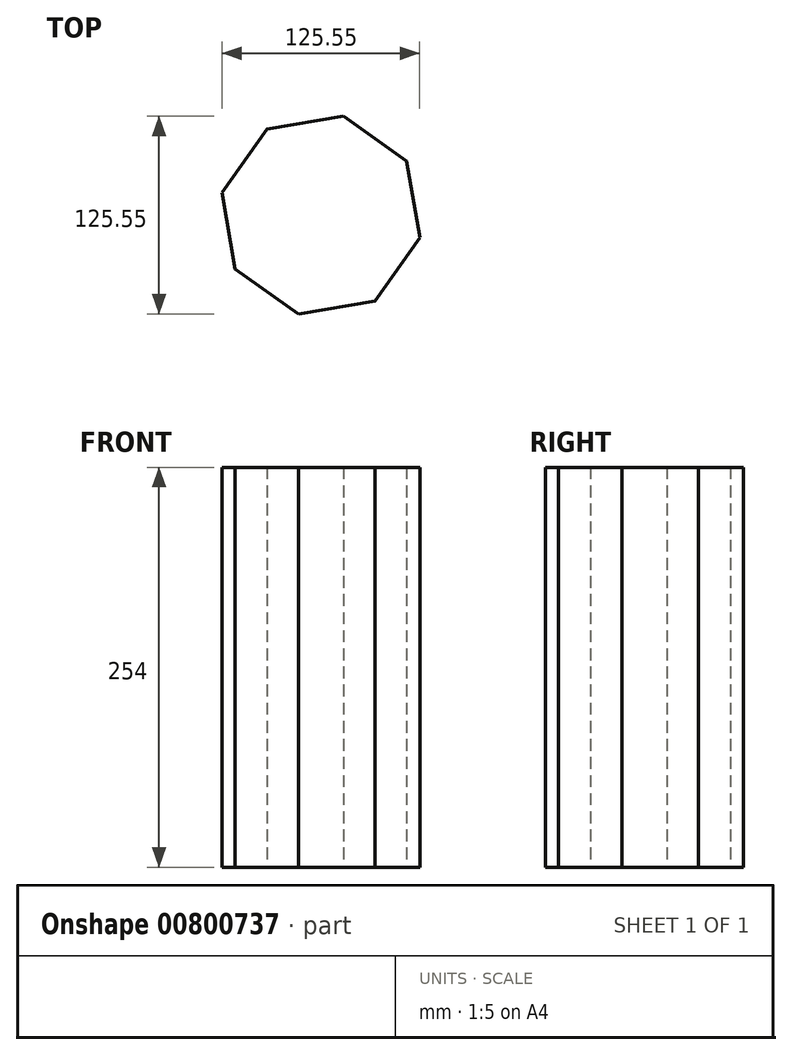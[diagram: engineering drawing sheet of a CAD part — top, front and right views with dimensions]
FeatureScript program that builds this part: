
annotation { "Feature Type Name" : "Feature", "Feature Type Description" : "" }
export const myFeature = defineFeature(function(context is Context, id is Id, definition is map)
    precondition{}
    {
        {
            var Q0;
            Q0=qCreatedBy(makeId("Top.planeOp"),FACE);
            var sketch = newSketch(context, id + "F0", { "sketchPlane" : qUnion([Q0])});
            skCircle(sketch, "E0.cCircle", {"center": v(-30.55, -6.8) * mm, "radius": 59.5 * mm, "construction": true});
            skLineSegment(sketch, "E0.0", {"start": v(-16.2, 55.98) * mm, "end": v(23.98, 27.44) * mm});
            skLineSegment(sketch, "E0.1", {"start": v(23.98, 27.44) * mm, "end": v(32.22, -21.15) * mm});
            skLineSegment(sketch, "E0.2", {"start": v(32.22, -21.15) * mm, "end": v(3.69, -61.33) * mm});
            skLineSegment(sketch, "E0.3", {"start": v(3.69, -61.33) * mm, "end": v(-44.9, -69.57) * mm});
            skLineSegment(sketch, "E0.4", {"start": v(-44.9, -69.57) * mm, "end": v(-85.09, -41.04) * mm});
            skLineSegment(sketch, "E0.5", {"start": v(-85.09, -41.04) * mm, "end": v(-93.33, 7.55) * mm});
            skLineSegment(sketch, "E0.6", {"start": v(-93.33, 7.55) * mm, "end": v(-64.8, 47.74) * mm});
            skLineSegment(sketch, "E0.7", {"start": v(-64.8, 47.74) * mm, "end": v(-16.2, 55.98) * mm});
            skPoint(sketch, "E0.0.midPoint", {"position": v(3.9, 41.71) * mm});
            skSolve(sketch);
        }
        {
            var Q0;
            Q0 = qSketchRegion(id + "F0", true);
            extrude(context, id + "F1", {"entities" : qUnion([Q0]), "depth" : 254 * mm, "offsetDistance" : 25.4 * mm});
        }
    });
